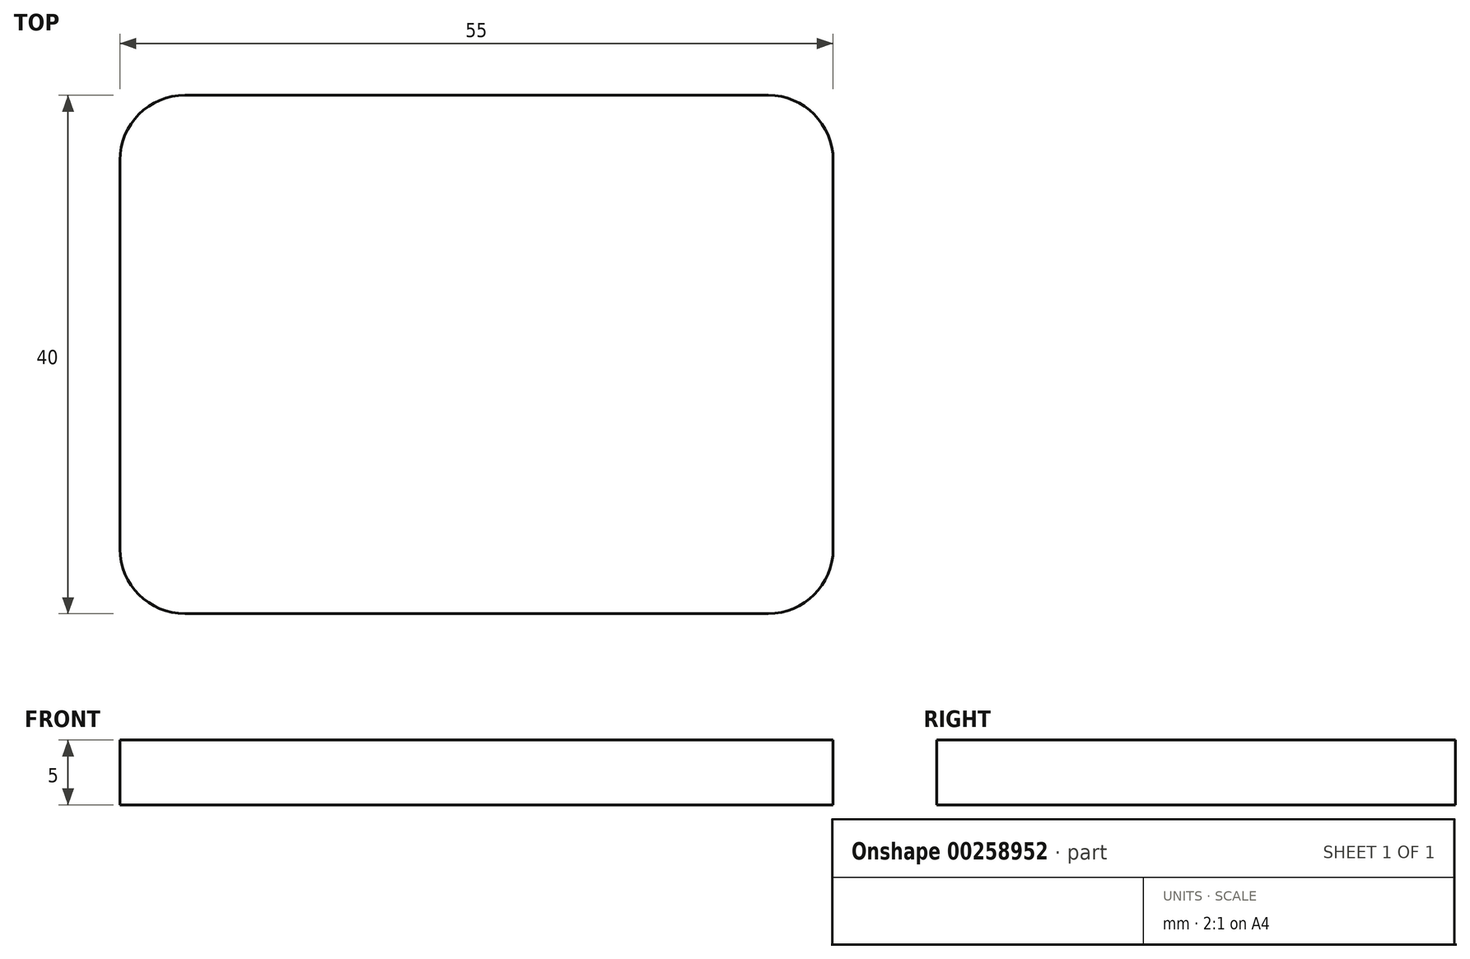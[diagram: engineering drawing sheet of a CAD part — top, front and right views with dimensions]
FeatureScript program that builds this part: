
annotation { "Feature Type Name" : "Feature", "Feature Type Description" : "" }
export const myFeature = defineFeature(function(context is Context, id is Id, definition is map)
    precondition{}
    {
        {
            var Q0;
            Q0=qCreatedBy(makeId("Top.planeOp"),FACE);
            var sketch = newSketch(context, id + "F0", { "sketchPlane" : qUnion([Q0])});
            skLineSegment(sketch, "E0.bottom", {"start": v(22.5, -20) * mm, "end": v(-22.5, -20) * mm});
            skLineSegment(sketch, "E0.top", {"start": v(22.5, 20) * mm, "end": v(-22.5, 20) * mm});
            skLineSegment(sketch, "E0.left", {"start": v(27.5, -15) * mm, "end": v(27.5, 15) * mm});
            skLineSegment(sketch, "E0.right", {"start": v(-27.5, -15) * mm, "end": v(-27.5, 15) * mm});
            skPoint(sketch, "E0.middle", {"position": v(0, 0) * mm});
            skPoint(sketch, "E1.visualSharp", {"position": v(-27.5, 20) * mm});
            skArc(sketch, "E1.filletArc", {"start": v(-22.5, 20) * mm, "mid": v(-26.04, 18.54) * mm, "end": v(-27.5, 15) * mm});
            skPoint(sketch, "E2.visualSharp", {"position": v(-27.5, -20) * mm});
            skArc(sketch, "E2.filletArc", {"start": v(-27.5, -15) * mm, "mid": v(-26.04, -18.54) * mm, "end": v(-22.5, -20) * mm});
            skPoint(sketch, "E3.visualSharp", {"position": v(27.5, -20) * mm});
            skArc(sketch, "E3.filletArc", {"start": v(22.5, -20) * mm, "mid": v(26.04, -18.54) * mm, "end": v(27.5, -15) * mm});
            skPoint(sketch, "E4.visualSharp", {"position": v(27.5, 20) * mm});
            skArc(sketch, "E4.filletArc", {"start": v(27.5, 15) * mm, "mid": v(26.04, 18.54) * mm, "end": v(22.5, 20) * mm});
            skSolve(sketch);
        }
        {
            var Q0;
            Q0 = qSketchRegion(id + "F0", true);
            extrude(context, id + "F1", {"entities" : qUnion([Q0]), "depth" : 5 * mm});
        }
    });
